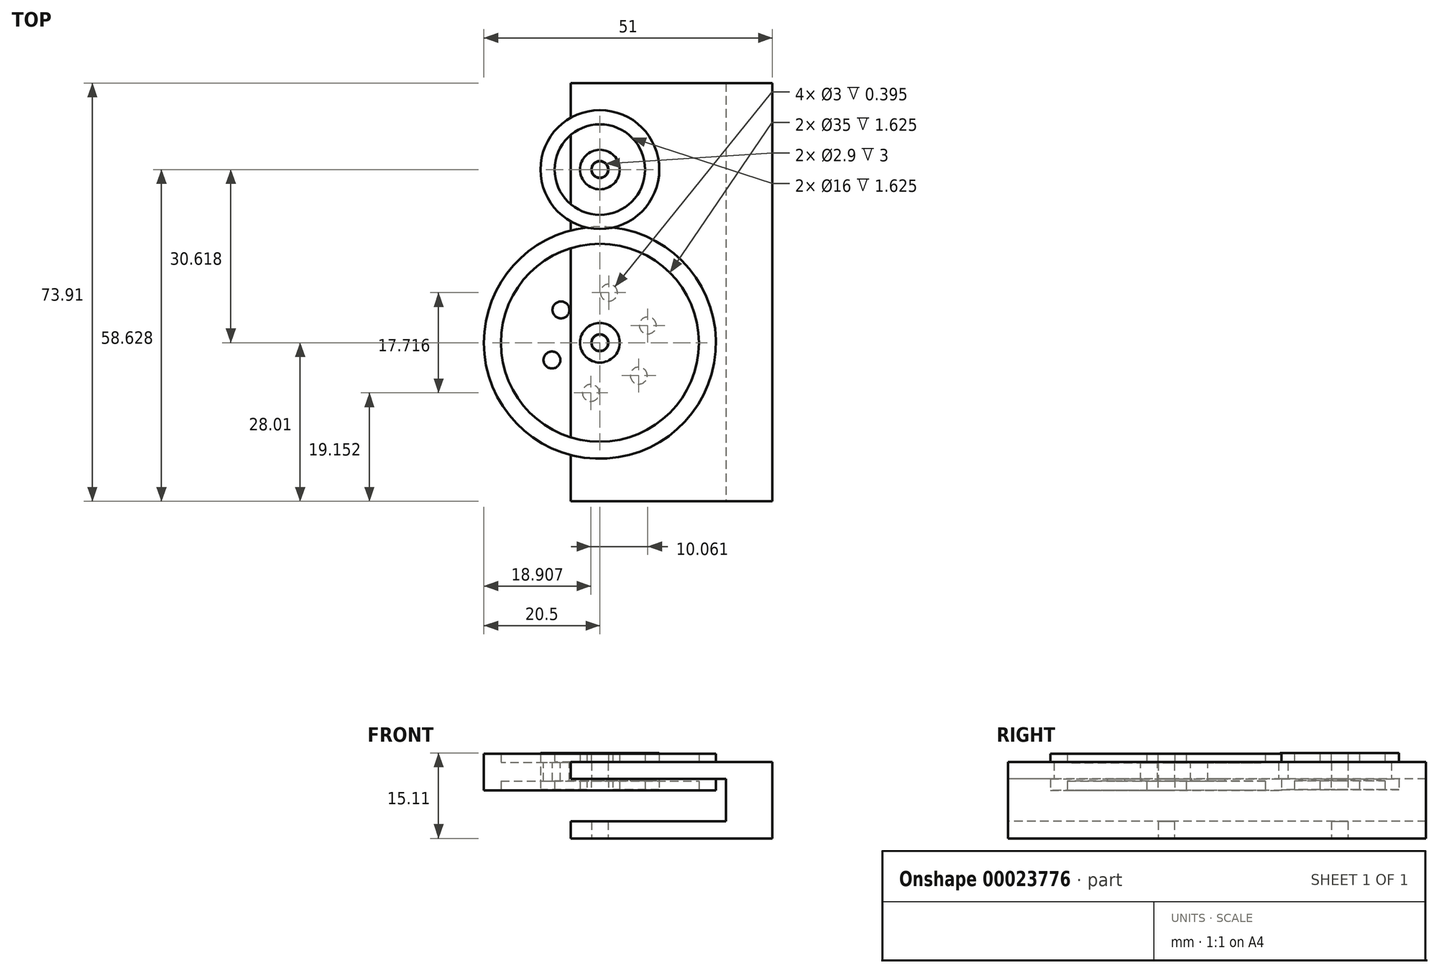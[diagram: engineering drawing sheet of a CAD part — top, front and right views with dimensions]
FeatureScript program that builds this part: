
annotation { "Feature Type Name" : "Feature", "Feature Type Description" : "" }
export const myFeature = defineFeature(function(context is Context, id is Id, definition is map)
    precondition{}
    {
        {
            var Q0;
            Q0=qCreatedBy(makeId("Front.planeOp"),FACE);
            var sketch = newSketch(context, id + "F0", { "sketchPlane" : qUnion([Q0])});
            skLineSegment(sketch, "E0", {"start": v(0, 0) * mm, "end": v(0, 22.56) * mm, "construction": true});
            skLineSegment(sketch, "E1", {"start": v(-1.5, 14.98) * mm, "end": v(-1.5, 8.48) * mm});
            skLineSegment(sketch, "E2", {"start": v(-1.5, 8.48) * mm, "end": v(-3.5, 8.48) * mm});
            skLineSegment(sketch, "E3", {"start": v(-3.5, 8.48) * mm, "end": v(-3.5, 10.1) * mm});
            skLineSegment(sketch, "E4", {"start": v(-3.5, 10.1) * mm, "end": v(-17.5, 10.1) * mm});
            skLineSegment(sketch, "E5", {"start": v(-17.5, 10.1) * mm, "end": v(-17.5, 8.48) * mm});
            skLineSegment(sketch, "E6", {"start": v(-17.5, 8.48) * mm, "end": v(-20.5, 8.48) * mm});
            skLineSegment(sketch, "E7", {"start": v(-20.5, 8.48) * mm, "end": v(-20.5, 14.98) * mm});
            skLineSegment(sketch, "E8", {"start": v(-20.5, 14.98) * mm, "end": v(-17.5, 14.98) * mm});
            skLineSegment(sketch, "E9", {"start": v(-17.5, 14.98) * mm, "end": v(-17.5, 13.36) * mm});
            skLineSegment(sketch, "E10", {"start": v(-17.5, 13.36) * mm, "end": v(-3.5, 13.36) * mm});
            skLineSegment(sketch, "E11", {"start": v(-3.5, 13.36) * mm, "end": v(-3.5, 14.98) * mm});
            skLineSegment(sketch, "E12", {"start": v(-3.5, 14.98) * mm, "end": v(-1.5, 14.98) * mm});
            skSolve(sketch);
        }
        {
            var Q0;
            Q0=makeQuery(id+"F0.imprint","IMPRINT",FACE,{"disambiguationData":[TD([[makeQuery(id+"F0.imprint","IMPRINT",EDGE,{"derivedFrom":sQuery(id+"F0.wireOp",EDGE,"E1")}),-1.0]])]});
            var Q1;
            Q1=sQuery(id+"F0.wireOp",EDGE,"E0");
            revolve(context, id + "F1", {"entities" : qUnion([Q0]), "axis" : qUnion([Q1]), "revolveType" : RevolveType.FULL});
        }
        {
            var Q0;
            Q0=makeQuery(id+"F1.opRevolve","SWEPT_FACE",FACE,{"disambiguationData":[OSD([sQuery(id+"F0.wireOp",EDGE,"E10")])]});
            var sketch = newSketch(context, id + "F2", { "sketchPlane" : qUnion([Q0])});
            skCircle(sketch, "E13", {"center": v(-6.87, 5.8) * mm, "radius": 1.5 * mm});
            skCircle(sketch, "E14.1.0", {"center": v(-8.47, -3.05) * mm, "radius": 1.5 * mm});
            skCircle(sketch, "E14.2.0", {"center": v(-1.6, -8.86) * mm, "radius": 1.5 * mm});
            skCircle(sketch, "E14.3.0", {"center": v(6.87, -5.8) * mm, "radius": 1.5 * mm});
            skCircle(sketch, "E14.4.0", {"center": v(8.47, 3.05) * mm, "radius": 1.5 * mm});
            skCircle(sketch, "E14.5.0", {"center": v(1.6, 8.86) * mm, "radius": 1.5 * mm});
            skPoint(sketch, "E14.center", {"position": v(0, 0) * mm});
            skSolve(sketch);
        }
        {
            var Q0;
            Q0=makeQuery(id+"F2.imprint","IMPRINT",FACE,{"disambiguationData":[TD([[makeQuery(id+"F2.imprint","IMPRINT",EDGE,{"derivedFrom":sQuery(id+"F2.wireOp",EDGE,"E14.2.0")}),1.0]])]});
            var Q1;
            Q1=makeQuery(id+"F2.imprint","IMPRINT",FACE,{"disambiguationData":[TD([[makeQuery(id+"F2.imprint","IMPRINT",EDGE,{"derivedFrom":sQuery(id+"F2.wireOp",EDGE,"E14.1.0")}),1.0]])]});
            var Q2;
            Q2=makeQuery(id+"F2.imprint","IMPRINT",FACE,{"disambiguationData":[TD([[makeQuery(id+"F2.imprint","IMPRINT",EDGE,{"derivedFrom":sQuery(id+"F2.wireOp",EDGE,"E13")}),1.0]])]});
            var Q3;
            Q3=makeQuery(id+"F2.imprint","IMPRINT",FACE,{"disambiguationData":[TD([[makeQuery(id+"F2.imprint","IMPRINT",EDGE,{"derivedFrom":sQuery(id+"F2.wireOp",EDGE,"E14.5.0")}),1.0]])]});
            var Q4;
            Q4=makeQuery(id+"F2.imprint","IMPRINT",FACE,{"disambiguationData":[TD([[makeQuery(id+"F2.imprint","IMPRINT",EDGE,{"derivedFrom":sQuery(id+"F2.wireOp",EDGE,"E14.4.0")}),1.0]])]});
            var Q5;
            Q5=makeQuery(id+"F2.imprint","IMPRINT",FACE,{"disambiguationData":[TD([[makeQuery(id+"F2.imprint","IMPRINT",EDGE,{"derivedFrom":sQuery(id+"F2.wireOp",EDGE,"E14.3.0")}),1.0]])]});
            extrude(context, id + "F3", {"entities" : qUnion([Q0, Q1, Q2, Q3, Q4, Q5]), "operationType" : NewBodyOperationType.REMOVE, "oppositeDirection" : true, "depth" : 6.5 * mm});
        }
        {
            var Q0;
            Q0=qCreatedBy(makeId("Right.planeOp"),FACE);
            var sketch = newSketch(context, id + "F4", { "sketchPlane" : qUnion([Q0])});
            skLineSegment(sketch, "E15", {"start": v(30.62, -20.77) * mm, "end": v(30.62, 27.65) * mm, "construction": true});
            skLineSegment(sketch, "E16", {"start": v(29.12, 15.1) * mm, "end": v(29.12, 8.6) * mm});
            skLineSegment(sketch, "E17", {"start": v(29.12, 8.6) * mm, "end": v(27.12, 8.6) * mm});
            skLineSegment(sketch, "E18", {"start": v(27.12, 8.6) * mm, "end": v(27.12, 10.23) * mm});
            skLineSegment(sketch, "E19", {"start": v(27.12, 10.23) * mm, "end": v(22.62, 10.23) * mm});
            skLineSegment(sketch, "E20", {"start": v(22.62, 10.23) * mm, "end": v(22.62, 8.6) * mm});
            skLineSegment(sketch, "E21", {"start": v(22.62, 8.6) * mm, "end": v(20.12, 8.6) * mm});
            skLineSegment(sketch, "E22", {"start": v(20.12, 8.6) * mm, "end": v(20.12, 15.1) * mm});
            skLineSegment(sketch, "E23", {"start": v(20.12, 15.1) * mm, "end": v(22.62, 15.1) * mm});
            skLineSegment(sketch, "E24", {"start": v(22.62, 15.1) * mm, "end": v(22.62, 13.48) * mm});
            skLineSegment(sketch, "E25", {"start": v(22.62, 13.48) * mm, "end": v(27.12, 13.48) * mm});
            skLineSegment(sketch, "E26", {"start": v(27.12, 13.48) * mm, "end": v(27.12, 15.1) * mm});
            skLineSegment(sketch, "E27", {"start": v(27.12, 15.1) * mm, "end": v(29.12, 15.1) * mm});
            skSolve(sketch);
        }
        {
            var Q0;
            Q0 = qSketchRegion(id + "F4", true);
            var Q1;
            Q1=sQuery(id+"F4.wireOp",EDGE,"E15");
            revolve(context, id + "F5", {"entities" : qUnion([Q0]), "axis" : qUnion([Q1]), "revolveType" : RevolveType.FULL});
        }
        {
            var Q0;
            Q0=qCreatedBy(makeId("Top.planeOp"),FACE);
            var sketch = newSketch(context, id + "F6", { "sketchPlane" : qUnion([Q0])});
            skLineSegment(sketch, "E28.bottom", {"start": v(-5.13, 45.9) * mm, "end": v(30.5, 45.9) * mm});
            skLineSegment(sketch, "E28.top", {"start": v(-5.13, -28) * mm, "end": v(30.5, -28) * mm});
            skLineSegment(sketch, "E28.left", {"start": v(-5.13, 45.9) * mm, "end": v(-5.13, -28) * mm});
            skLineSegment(sketch, "E28.right", {"start": v(30.5, 45.9) * mm, "end": v(30.5, -28) * mm});
            skCircle(sketch, "E29", {"center": v(0, 0) * mm, "radius": 1.45 * mm});
            skCircle(sketch, "E30", {"center": v(0, 30.62) * mm, "radius": 1.45 * mm});
            skSolve(sketch);
        }
        {
            var Q0;
            Q0 = qSketchRegion(id + "F6", true);
            extrude(context, id + "F7", {"entities" : qUnion([Q0]), "depth" : 3 * mm});
        }
        {
            var Q0;
            Q0=makeQuery(id+"F7.opExtrude","CAP_FACE",FACE,{"disambiguationData":[OSD([sQuery(id+"F6.wireOp",EDGE,"E28.bottom"),sQuery(id+"F6.wireOp",EDGE,"E28.top"),sQuery(id+"F6.wireOp",EDGE,"E28.left"),sQuery(id+"F6.wireOp",EDGE,"E28.right"),sQuery(id+"F6.wireOp",EDGE,"E29"),sQuery(id+"F6.wireOp",EDGE,"E30")])],"isStart":false});
            var sketch = newSketch(context, id + "F8", { "sketchPlane" : qUnion([Q0])});
            skLineSegment(sketch, "E31.bottom", {"start": v(22.3, 45.9) * mm, "end": v(30.5, 45.9) * mm});
            skLineSegment(sketch, "E31.top", {"start": v(22.3, -28) * mm, "end": v(30.5, -28) * mm});
            skLineSegment(sketch, "E31.left", {"start": v(22.3, 45.9) * mm, "end": v(22.3, -28) * mm});
            skLineSegment(sketch, "E31.right", {"start": v(30.5, 45.9) * mm, "end": v(30.5, -28) * mm});
            skSolve(sketch);
        }
        {
            var Q0;
            Q0 = qSketchRegion(id + "F8", true);
            extrude(context, id + "F9", {"entities" : qUnion([Q0]), "operationType" : NewBodyOperationType.ADD, "depth" : 7.5 * mm});
        }
        {
            var Q0;
            Q0=makeQuery(id+"F9.opExtrude","CAP_FACE",FACE,{"disambiguationData":[OSD([sQuery(id+"F8.wireOp",EDGE,"E31.bottom"),sQuery(id+"F8.wireOp",EDGE,"E31.top"),sQuery(id+"F8.wireOp",EDGE,"E31.left"),sQuery(id+"F8.wireOp",EDGE,"E31.right")])],"isStart":false});
            var sketch = newSketch(context, id + "F10", { "sketchPlane" : qUnion([Q0])});
            skLineSegment(sketch, "E32.bottom", {"start": v(30.5, 45.9) * mm, "end": v(-5.13, 45.9) * mm});
            skLineSegment(sketch, "E32.top", {"start": v(30.5, -28) * mm, "end": v(-5.13, -28) * mm});
            skLineSegment(sketch, "E32.left", {"start": v(30.5, 45.9) * mm, "end": v(30.5, -28) * mm});
            skLineSegment(sketch, "E32.right", {"start": v(-5.13, 45.9) * mm, "end": v(-5.13, -28) * mm});
            skCircle(sketch, "E33", {"center": v(0, 0) * mm, "radius": 1.45 * mm});
            skCircle(sketch, "E34", {"center": v(0, 30.62) * mm, "radius": 1.45 * mm});
            skSolve(sketch);
        }
        {
            var Q0;
            Q0 = qSketchRegion(id + "F10", true);
            extrude(context, id + "F11", {"entities" : qUnion([Q0]), "operationType" : NewBodyOperationType.ADD, "depth" : 3 * mm});
        }
    });
